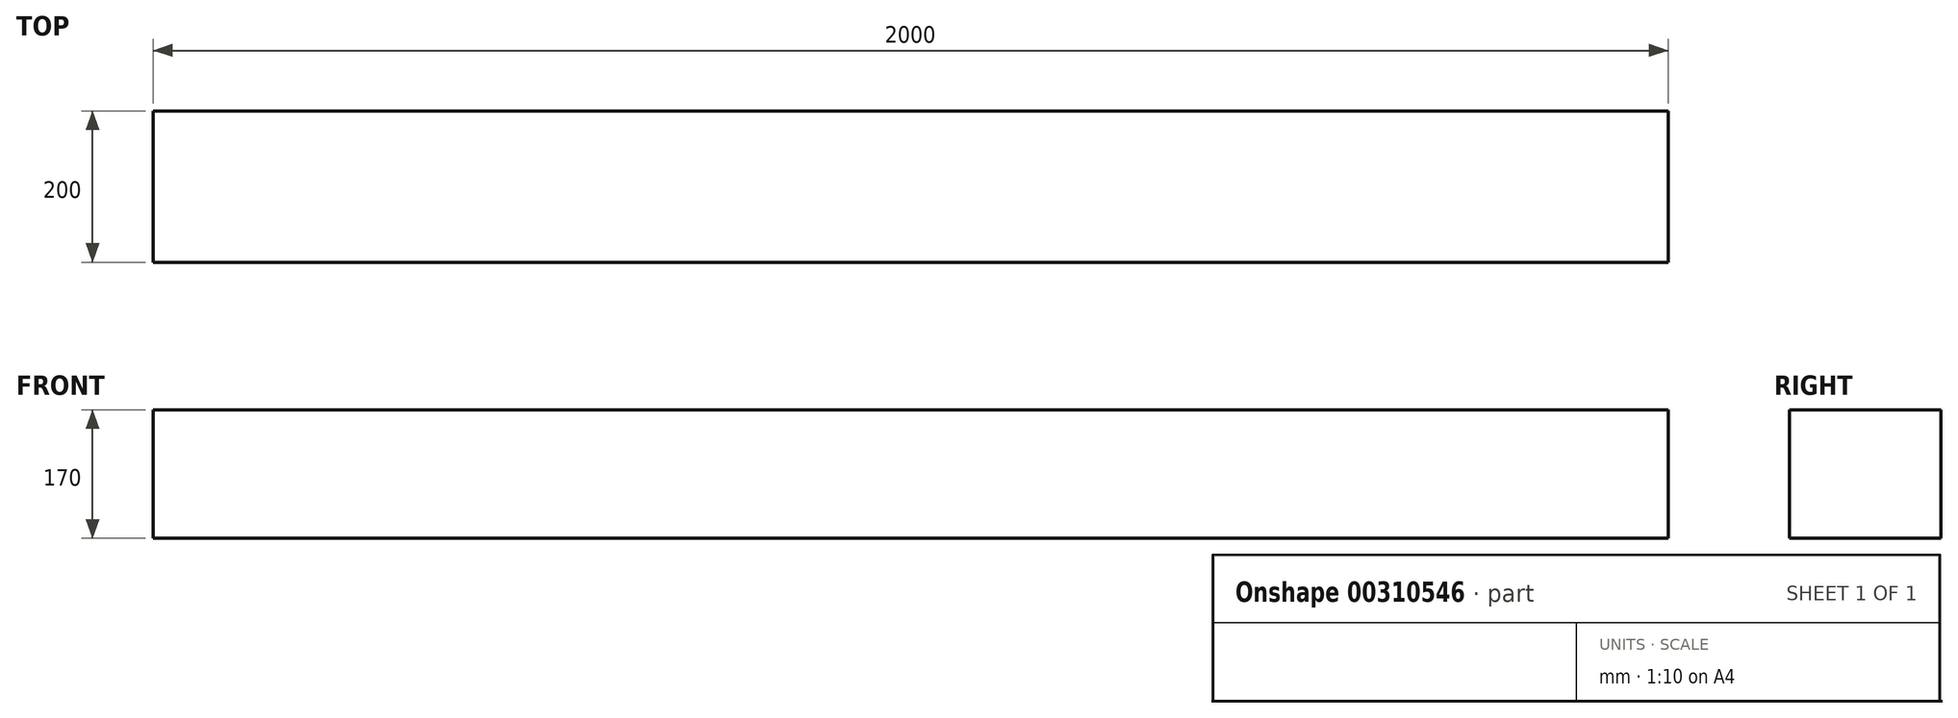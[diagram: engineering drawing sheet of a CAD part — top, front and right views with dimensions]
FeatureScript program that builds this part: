
annotation { "Feature Type Name" : "Feature", "Feature Type Description" : "" }
export const myFeature = defineFeature(function(context is Context, id is Id, definition is map)
    precondition{}
    {
        {
            var Q0;
            Q0=qCreatedBy(makeId("Front.planeOp"),FACE);
            var sketch = newSketch(context, id + "F0", { "sketchPlane" : qUnion([Q0])});
            skLineSegment(sketch, "E0.bottom", {"start": v(0, 0) * mm, "end": v(-2000, 0) * mm});
            skLineSegment(sketch, "E0.top", {"start": v(0, -170) * mm, "end": v(-2000, -170) * mm});
            skLineSegment(sketch, "E0.left", {"start": v(0, 0) * mm, "end": v(0, -170) * mm});
            skLineSegment(sketch, "E0.right", {"start": v(-2000, 0) * mm, "end": v(-2000, -170) * mm});
            skSolve(sketch);
        }
        {
            var Q0;
            Q0=makeQuery(id+"F0.imprint","IMPRINT",FACE,{"disambiguationData":[TD([[makeQuery(id+"F0.imprint","IMPRINT",EDGE,{"derivedFrom":sQuery(id+"F0.wireOp",EDGE,"E0.bottom")}),1.0]])]});
            extrude(context, id + "F1", {"entities" : qUnion([Q0]), "depth" : 200 * mm});
        }
    });
